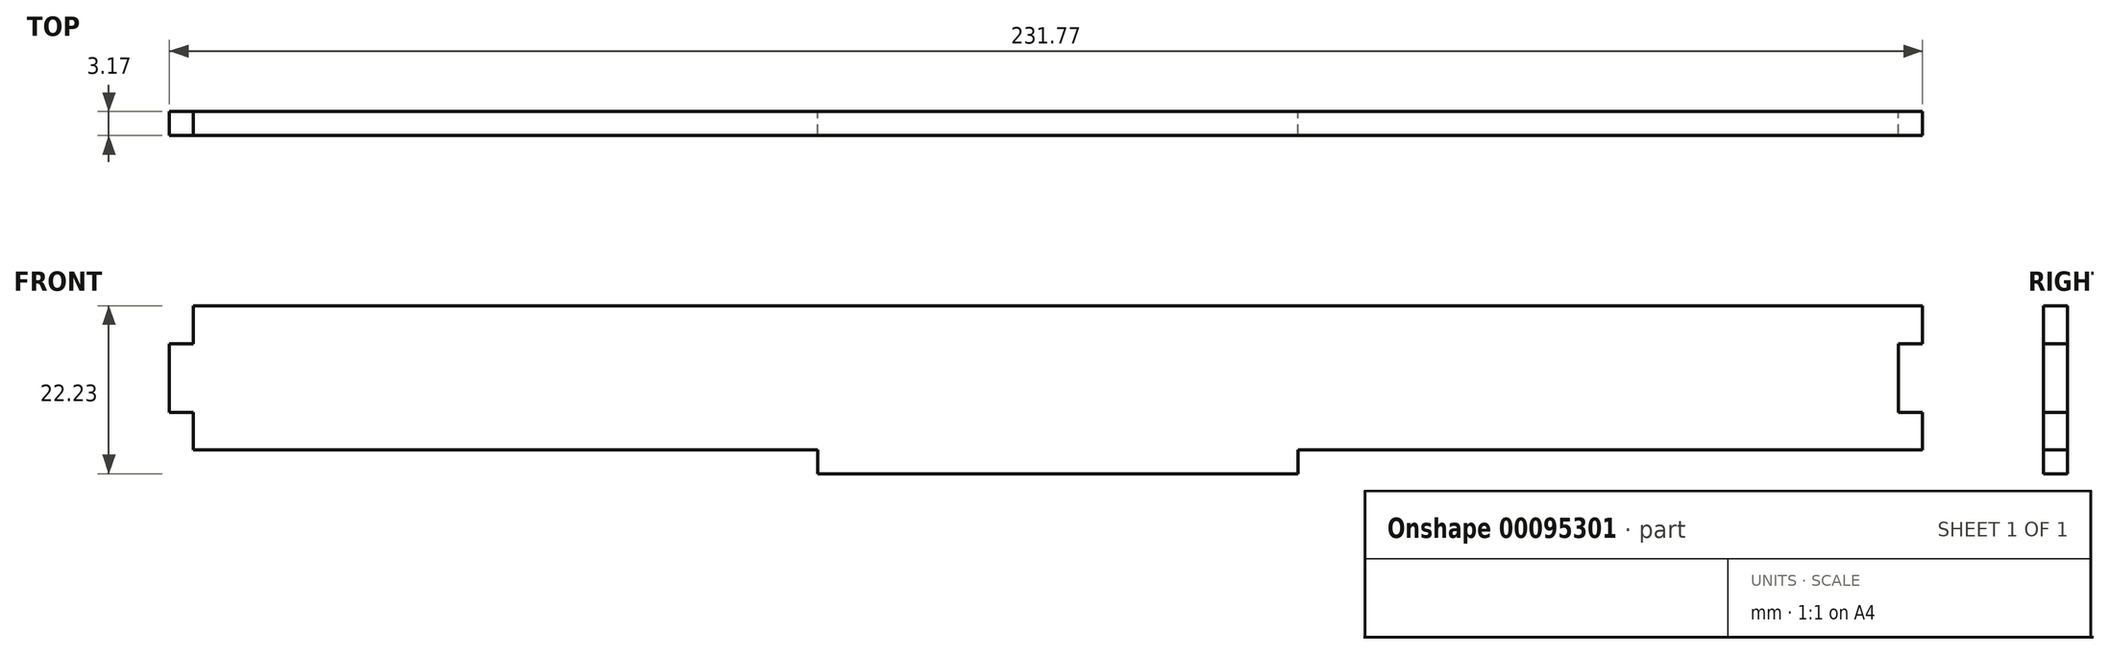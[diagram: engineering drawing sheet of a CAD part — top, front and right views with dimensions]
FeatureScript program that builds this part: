
annotation { "Feature Type Name" : "Feature", "Feature Type Description" : "" }
export const myFeature = defineFeature(function(context is Context, id is Id, definition is map)
    precondition{}
    {
        {
            var Q0;
            Q0=qCreatedBy(makeId("Front.planeOp"),FACE);
            var sketch = newSketch(context, id + "F0", { "sketchPlane" : qUnion([Q0])});
            skLineSegment(sketch, "E0.bottom", {"start": v(114.3, 9.53) * mm, "end": v(-114.3, 9.53) * mm});
            skLineSegment(sketch, "E0.top", {"start": v(114.3, -9.52) * mm, "end": v(-114.3, -9.52) * mm});
            skLineSegment(sketch, "E0.left", {"start": v(114.3, 9.53) * mm, "end": v(114.3, -9.52) * mm});
            skLineSegment(sketch, "E0.right", {"start": v(-114.3, 9.53) * mm, "end": v(-114.3, -9.53) * mm});
            skPoint(sketch, "E0.middle", {"position": v(0, 0) * mm});
            skLineSegment(sketch, "E1.bottom", {"start": v(-114.3, -9.52) * mm, "end": v(-63.5, -9.52) * mm});
            skLineSegment(sketch, "E1.top", {"start": v(-114.3, -12.7) * mm, "end": v(-63.5, -12.7) * mm});
            skLineSegment(sketch, "E1.left", {"start": v(-114.3, -9.52) * mm, "end": v(-114.3, -12.7) * mm});
            skLineSegment(sketch, "E1.right", {"start": v(-63.5, -9.52) * mm, "end": v(-63.5, -12.7) * mm});
            skLineSegment(sketch, "E2.bottom", {"start": v(114.3, -9.52) * mm, "end": v(63.5, -9.52) * mm});
            skLineSegment(sketch, "E2.top", {"start": v(114.3, -12.7) * mm, "end": v(63.5, -12.7) * mm});
            skLineSegment(sketch, "E2.left", {"start": v(114.3, -9.52) * mm, "end": v(114.3, -12.7) * mm});
            skLineSegment(sketch, "E2.right", {"start": v(63.5, -9.52) * mm, "end": v(63.5, -12.7) * mm});
            skLineSegment(sketch, "E3.bottom", {"start": v(31.75, -12.7) * mm, "end": v(-31.75, -12.7) * mm});
            skLineSegment(sketch, "E3.top", {"start": v(31.75, -6.35) * mm, "end": v(-31.75, -6.35) * mm});
            skLineSegment(sketch, "E3.left", {"start": v(31.75, -12.7) * mm, "end": v(31.75, -6.35) * mm});
            skLineSegment(sketch, "E3.right", {"start": v(-31.75, -12.7) * mm, "end": v(-31.75, -6.35) * mm});
            skPoint(sketch, "E3.middle", {"position": v(0, -9.52) * mm});
            skLineSegment(sketch, "E4.bottom", {"start": v(-114.3, 4.48) * mm, "end": v(-117.48, 4.48) * mm});
            skLineSegment(sketch, "E4.top", {"start": v(-114.3, -4.58) * mm, "end": v(-117.48, -4.58) * mm});
            skLineSegment(sketch, "E4.left", {"start": v(-114.3, 4.48) * mm, "end": v(-114.3, -4.58) * mm});
            skLineSegment(sketch, "E4.right", {"start": v(-117.48, 4.48) * mm, "end": v(-117.48, -4.58) * mm});
            skLineSegment(sketch, "E5.bottom", {"start": v(111.13, 4.48) * mm, "end": v(114.3, 4.48) * mm});
            skLineSegment(sketch, "E5.top", {"start": v(111.13, -4.58) * mm, "end": v(114.3, -4.58) * mm});
            skLineSegment(sketch, "E5.left", {"start": v(114.3, 4.48) * mm, "end": v(114.3, -4.58) * mm});
            skLineSegment(sketch, "E5.right", {"start": v(111.13, 4.48) * mm, "end": v(111.13, -4.58) * mm});
            skSolve(sketch);
        }
        {
            var Q0;
            {var subQ5=sQuery(id+"F0.wireOp",EDGE,"E3.bottom");Q0=makeQuery(id+"F0.imprint","IMPRINT",FACE,{"disambiguationData":[TD([[makeQuery(id+"F0.imprint","IMPRINT",EDGE,{"derivedFrom":subQ5}),-1.0]])]});}
            var Q1;
            Q1=makeQuery(id+"F0.imprint","IMPRINT",FACE,{"disambiguationData":[TD([[makeQuery(id+"F0.imprint","IMPRINT",EDGE,{"derivedFrom":sQuery(id+"F0.wireOp",EDGE,"E1.bottom")}),-1.0]])]});
            var Q2;
            Q2=makeQuery(id+"F0.imprint","IMPRINT",FACE,{"disambiguationData":[TD([[makeQuery(id+"F0.imprint","IMPRINT",EDGE,{"derivedFrom":sQuery(id+"F0.wireOp",EDGE,"E2.bottom")}),1.0]])]});
            var Q3;
            Q3=makeQuery(id+"F0.imprint","IMPRINT",FACE,{"disambiguationData":[TD([[makeQuery(id+"F0.imprint","IMPRINT",EDGE,{"derivedFrom":sQuery(id+"F0.wireOp",EDGE,"E4.bottom")}),1.0]])]});
            var Q4;
            {var subQ5=sQuery(id+"F0.wireOp",EDGE,"E3.top");Q4=makeQuery(id+"F0.imprint","IMPRINT",FACE,{"disambiguationData":[TD([[makeQuery(id+"F0.imprint","IMPRINT",EDGE,{"derivedFrom":subQ5}),1.0]])]});}
            var Q5;
            {var subQ3=sQuery(id+"F0.wireOp",EDGE,"E0.bottom");Q5=makeQuery(id+"F0.imprint","IMPRINT",FACE,{"disambiguationData":[TD([[makeQuery(id+"F0.imprint","IMPRINT",EDGE,{"derivedFrom":subQ3}),1.0]])]});}
            extrude(context, id + "F1", {"entities" : qUnion([Q0, Q1, Q2, Q3, Q4, Q5]), "depth" : 3.17 * mm});
        }
    });
